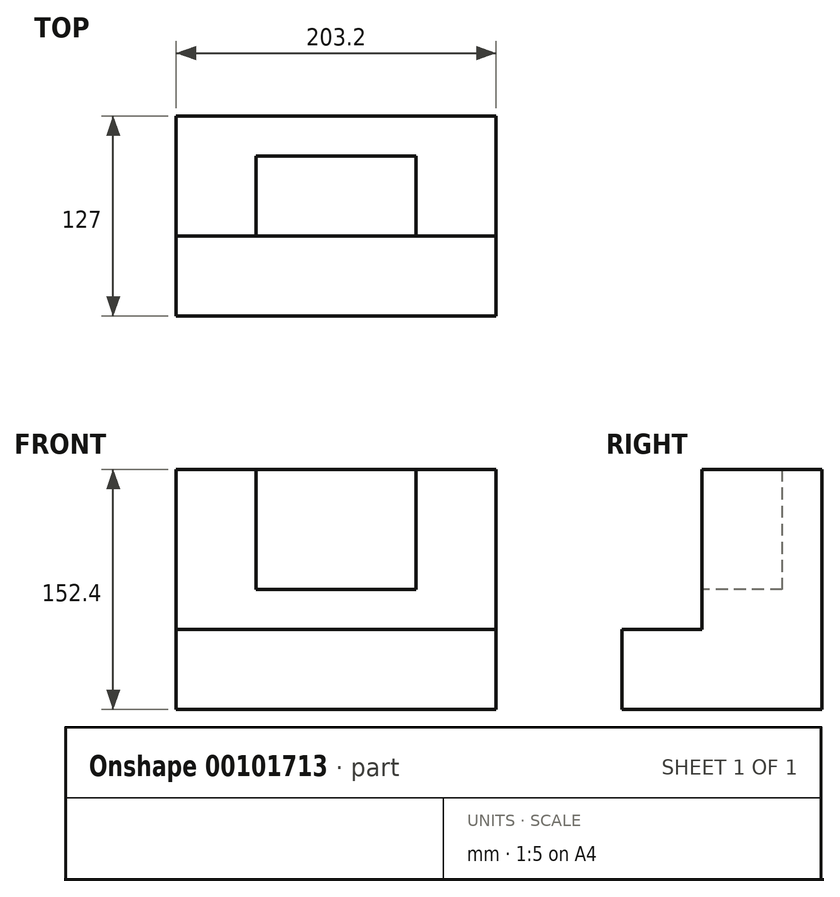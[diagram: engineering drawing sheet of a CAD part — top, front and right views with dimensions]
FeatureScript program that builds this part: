
annotation { "Feature Type Name" : "Feature", "Feature Type Description" : "" }
export const myFeature = defineFeature(function(context is Context, id is Id, definition is map)
    precondition{}
    {
        {
            var Q0;
            Q0=qCreatedBy(makeId("Front.planeOp"),FACE);
            var sketch = newSketch(context, id + "F0", { "sketchPlane" : qUnion([Q0])});
            skLineSegment(sketch, "E0", {"start": v(-100.88, -5.89) * mm, "end": v(-100.88, -56.69) * mm});
            skLineSegment(sketch, "E1", {"start": v(-100.88, -56.69) * mm, "end": v(102.32, -56.69) * mm});
            skLineSegment(sketch, "E2", {"start": v(102.32, -56.69) * mm, "end": v(102.32, -5.89) * mm});
            skLineSegment(sketch, "E3", {"start": v(102.32, -5.89) * mm, "end": v(-100.88, -5.89) * mm});
            skSolve(sketch);
        }
        {
            var Q0;
            Q0=makeQuery(id+"F0.imprint","IMPRINT",FACE,{"disambiguationData":[TD([[makeQuery(id+"F0.imprint","IMPRINT",EDGE,{"derivedFrom":sQuery(id+"F0.wireOp",EDGE,"E0")}),1.0]])]});
            extrude(context, id + "F1", {"entities" : qUnion([Q0]), "depth" : 127 * mm});
        }
        {
            var Q0;
            Q0=makeQuery(id+"F1.opExtrude","SWEPT_FACE",FACE,{"disambiguationData":[OSD([sQuery(id+"F0.wireOp",EDGE,"E3")])]});
            var sketch = newSketch(context, id + "F2", { "sketchPlane" : qUnion([Q0])});
            skLineSegment(sketch, "E4.bottom", {"start": v(-100.88, 0) * mm, "end": v(-50.08, 0) * mm});
            skLineSegment(sketch, "E4.top", {"start": v(-100.88, -76.2) * mm, "end": v(-50.08, -76.2) * mm});
            skLineSegment(sketch, "E4.left", {"start": v(-100.88, 0) * mm, "end": v(-100.88, -76.2) * mm});
            skLineSegment(sketch, "E4.right", {"start": v(-50.08, 0) * mm, "end": v(-50.08, -76.2) * mm});
            skSolve(sketch);
        }
        {
            var Q0;
            Q0=makeQuery(id+"F2.imprint","IMPRINT",FACE,{"disambiguationData":[TD([[makeQuery(id+"F2.imprint","IMPRINT",EDGE,{"derivedFrom":sQuery(id+"F2.wireOp",EDGE,"E4.bottom")}),1.0]])]});
            extrude(context, id + "F3", {"entities" : qUnion([Q0]), "operationType" : NewBodyOperationType.ADD, "depth" : 101.6 * mm});
        }
        {
            var Q0;
            Q0=makeQuery(id+"F1.opExtrude","SWEPT_FACE",FACE,{"disambiguationData":[OSD([sQuery(id+"F0.wireOp",EDGE,"E3")])]});
            var sketch = newSketch(context, id + "F4", { "sketchPlane" : qUnion([Q0])});
            skLineSegment(sketch, "E5.bottom", {"start": v(102.32, 0) * mm, "end": v(51.52, 0) * mm});
            skLineSegment(sketch, "E5.top", {"start": v(102.32, -76.2) * mm, "end": v(51.52, -76.2) * mm});
            skLineSegment(sketch, "E5.left", {"start": v(102.32, 0) * mm, "end": v(102.32, -76.2) * mm});
            skLineSegment(sketch, "E5.right", {"start": v(51.52, 0) * mm, "end": v(51.52, -76.2) * mm});
            skSolve(sketch);
        }
        {
            var Q0;
            Q0=makeQuery(id+"F4.imprint","IMPRINT",FACE,{"disambiguationData":[TD([[makeQuery(id+"F4.imprint","IMPRINT",EDGE,{"derivedFrom":sQuery(id+"F4.wireOp",EDGE,"E5.bottom")}),1.0]])]});
            extrude(context, id + "F5", {"entities" : qUnion([Q0]), "operationType" : NewBodyOperationType.ADD, "depth" : 101.6 * mm});
        }
        {
            var Q0;
            Q0=makeQuery(id+"F1.opExtrude","SWEPT_FACE",FACE,{"disambiguationData":[OSD([sQuery(id+"F0.wireOp",EDGE,"E3")])]});
            var sketch = newSketch(context, id + "F6", { "sketchPlane" : qUnion([Q0])});
            skLineSegment(sketch, "E6.bottom", {"start": v(-50.08, -25.4) * mm, "end": v(51.52, -25.4) * mm});
            skLineSegment(sketch, "E6.top", {"start": v(-50.08, -76.2) * mm, "end": v(51.52, -76.2) * mm});
            skLineSegment(sketch, "E6.left", {"start": v(-50.08, -25.4) * mm, "end": v(-50.08, -76.2) * mm});
            skLineSegment(sketch, "E6.right", {"start": v(51.52, -25.4) * mm, "end": v(51.52, -76.2) * mm});
            skSolve(sketch);
        }
        {
            var Q0;
            Q0=makeQuery(id+"F6.imprint","IMPRINT",FACE,{"disambiguationData":[TD([[makeQuery(id+"F6.imprint","IMPRINT",EDGE,{"derivedFrom":sQuery(id+"F6.wireOp",EDGE,"E6.bottom")}),-1.0]])]});
            extrude(context, id + "F7", {"entities" : qUnion([Q0]), "operationType" : NewBodyOperationType.ADD, "depth" : 25.4 * mm});
        }
        {
            var Q0;
            {var subQ0=sQuery(id+"F0.wireOp",EDGE,"E3");Q0=makeQuery(id+"F7.boolean.opBoolean","SPLIT",FACE,{"disambiguationData":[TD([makeQuery(id+"F3.opExtrude","SWEPT_FACE",FACE,{"disambiguationData":[OSD([sQuery(id+"F2.wireOp",EDGE,"E4.bottom")])]})])],"derivedFrom":makeQuery(id+"F1.opExtrude","SWEPT_FACE",FACE,{"disambiguationData":[OSD([subQ0])]})});}
            var sketch = newSketch(context, id + "F8", { "sketchPlane" : qUnion([Q0])});
            skLineSegment(sketch, "E7.bottom", {"start": v(-50.08, 0) * mm, "end": v(51.52, 0) * mm});
            skLineSegment(sketch, "E7.top", {"start": v(-50.08, -25.4) * mm, "end": v(51.52, -25.4) * mm});
            skLineSegment(sketch, "E7.left", {"start": v(-50.08, 0) * mm, "end": v(-50.08, -25.4) * mm});
            skLineSegment(sketch, "E7.right", {"start": v(51.52, 0) * mm, "end": v(51.52, -25.4) * mm});
            skSolve(sketch);
        }
        {
            var Q0;
            Q0=makeQuery(id+"F8.imprint","IMPRINT",FACE,{"disambiguationData":[TD([[makeQuery(id+"F8.imprint","IMPRINT",EDGE,{"derivedFrom":sQuery(id+"F8.wireOp",EDGE,"E7.bottom")}),1.0]])]});
            extrude(context, id + "F9", {"entities" : qUnion([Q0]), "operationType" : NewBodyOperationType.ADD, "depth" : 101.6 * mm});
        }
    });
